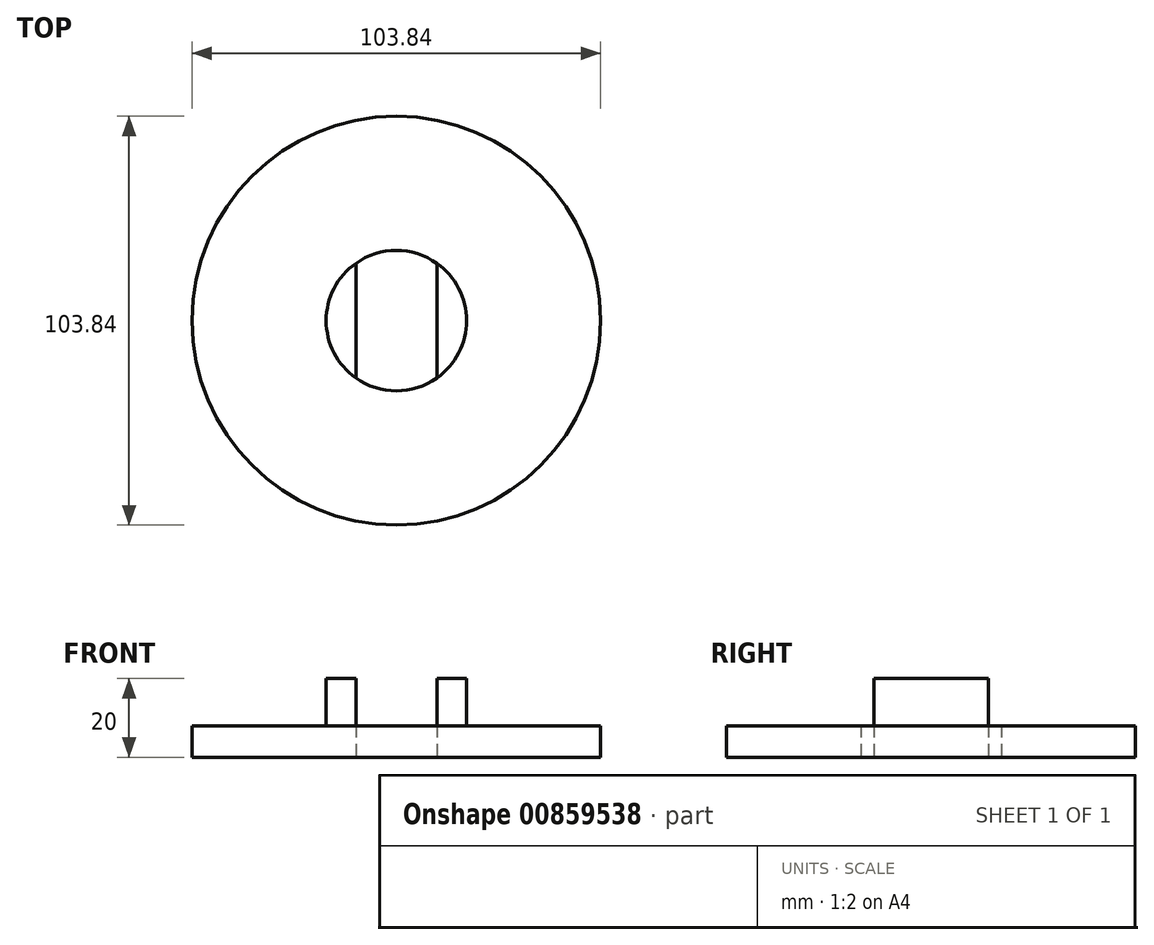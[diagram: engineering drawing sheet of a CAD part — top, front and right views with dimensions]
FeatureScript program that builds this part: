
annotation { "Feature Type Name" : "Feature", "Feature Type Description" : "" }
export const myFeature = defineFeature(function(context is Context, id is Id, definition is map)
    precondition{}
    {
        {
            var Q0;
            Q0=qCreatedBy(makeId("Top.planeOp"),FACE);
            var sketch = newSketch(context, id + "F0", { "sketchPlane" : qUnion([Q0])});
            skCircle(sketch, "E0", {"center": v(0, 0) * mm, "radius": 51.92 * mm});
            skCircle(sketch, "E1", {"center": v(0, 0) * mm, "radius": 17.83 * mm});
            skLineSegment(sketch, "E2", {"start": v(-10.3, 14.56) * mm, "end": v(-10.3, -14.56) * mm});
            skLineSegment(sketch, "E3.MirrorCS", {"start": v(10.3, 14.56) * mm, "end": v(10.3, -14.56) * mm});
            skSolve(sketch);
        }
        {
            var Q0;
            Q0=makeQuery(id+"F0.imprint","IMPRINT",FACE,{"disambiguationData":[TD([[makeQuery(id+"F0.imprint","IMPRINT",EDGE,{"derivedFrom":sQuery(id+"F0.wireOp",EDGE,"E0")}),1.0]])]});
            var Q1;
            {var subQ0=sQuery(id+"F0.wireOp",EDGE,"E2");Q1=makeQuery(id+"F0.imprint","IMPRINT",FACE,{"disambiguationData":[TD([[makeQuery(id+"F0.imprint","IMPRINT",EDGE,{"derivedFrom":subQ0}),-1.0]])]});}
            var Q2;
            {var subQ0=sQuery(id+"F0.wireOp",EDGE,"E3.MirrorCS");Q2=makeQuery(id+"F0.imprint","IMPRINT",FACE,{"disambiguationData":[TD([[makeQuery(id+"F0.imprint","IMPRINT",EDGE,{"derivedFrom":subQ0}),1.0]])]});}
            extrude(context, id + "F1", {"entities" : qUnion([Q0, Q1, Q2]), "depth" : 8 * mm, "offsetDistance" : 25 * mm});
        }
        {
            var Q0;
            {var subQ0=sQuery(id+"F0.wireOp",EDGE,"E2");Q0=makeQuery(id+"F0.imprint","IMPRINT",FACE,{"disambiguationData":[TD([[makeQuery(id+"F0.imprint","IMPRINT",EDGE,{"derivedFrom":subQ0}),-1.0]])]});}
            var Q1;
            {var subQ0=sQuery(id+"F0.wireOp",EDGE,"E3.MirrorCS");Q1=makeQuery(id+"F0.imprint","IMPRINT",FACE,{"disambiguationData":[TD([[makeQuery(id+"F0.imprint","IMPRINT",EDGE,{"derivedFrom":subQ0}),1.0]])]});}
            extrude(context, id + "F2", {"entities" : qUnion([Q0, Q1]), "operationType" : NewBodyOperationType.ADD, "depth" : 20 * mm, "offsetDistance" : 25 * mm});
        }
    });
